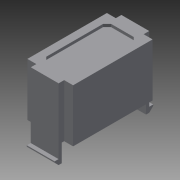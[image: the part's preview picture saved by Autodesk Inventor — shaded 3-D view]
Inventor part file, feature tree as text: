
AUTODESK INVENTOR PART (.ipt)
format: ipt  version: 2014 (Build 180170000, 170)  size: 151,040 bytes
history: native  units: mm
features: extrude x4, sketch x4, plane x1, chamfer x1, mirror x1
ambient origin geometry x8: Origin, YZ Plane, XZ Plane, XY Plane, X Axis, Y Axis, Z Axis, Center Point
bodies: Volumenkörper1 (feature_tree)
feature tree (11):
  extrude  "Extrusion1"  Depth=20.0mm
  plane  "Arbeitsebene2"
  extrude  "Extrusion2"  Depth=7.0mm
  extrude  "Extrusion3"  Depth=2.25mm
  extrude  "Extrusion4"  Depth=1.9mm
  chamfer  "Fase1"  Distance=1.9mm
  mirror  "Spiegeln1"
  sketch  "Skizze1"  dims[d0=11.5mm d1=20.0mm]
  sketch  "Skizze2"  dims[d2=13.3mm d3=0.0mm d4=7.0mm]
  sketch  "Skizze4"  dims[d5=1.4mm d6=2.25mm]
  sketch  "Skizze5"  dims[d7=2.25mm d8=1.9mm d9=1.9mm d10=3.25mm d11=3.25mm d12=1.0mm d13=1.0mm d14=1.0mm d15=1.0mm d16=1.0mm d17=1.0mm d18=1.0mm d19=1.0mm d20=0.7mm d21=0.0mm d32=0.8mm d34=4.5mm d35=0.0mm d36=1.3mm d37=1.0mm d38=0.0mm d39=1.0mm d40=2.0mm d41=45.0deg]
